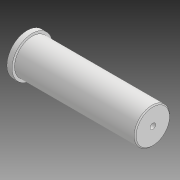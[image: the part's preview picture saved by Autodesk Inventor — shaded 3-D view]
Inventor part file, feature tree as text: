
AUTODESK INVENTOR PART (.ipt)
format: ipt  version: 2020 (Build 240168000, 168)  size: 102,400 bytes
history: native  units: mm
features: revolve x1, chamfer x1, sketch x1
ambient origin geometry x8: Origin, YZ Plane, XZ Plane, XY Plane, X Axis, Y Axis, Z Axis, Center Point
bodies: Solid1 (feature_tree)
feature tree (3):
  revolve  "Revolution1"  [1 undecoded]
  chamfer  "Chamfer1"  Distance=15.0mm
  sketch  "Sketch1"  dims[d0=2.7mm d1=4.5mm d2=15.0mm d3=5.0mm d4=17.4mm d5=2.5mm d6=118.5mm d7=90.0deg d8=1.0mm d9=2.0mm d10=45.0deg]
note: 1 required parameter value undecoded (feature->parameter linkage not recoverable at this tier; creation-order binding heuristic only, values carry confidence <= 0.55)
